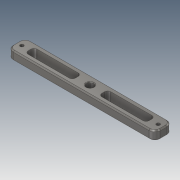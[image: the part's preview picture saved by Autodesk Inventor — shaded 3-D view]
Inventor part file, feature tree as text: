
AUTODESK INVENTOR PART (.ipt)
format: ipt  version: 2018.2 (Build 222227000, 227)  size: 164,864 bytes
history: native  units: mm
features: sketch x4, chamfer x3, extrude x2, mirror x1, hole x1, fillet x1
ambient origin geometry x8: Origin, YZ Plane, XZ Plane, XY Plane, X Axis, Y Axis, Z Axis, Center Point
bodies: Volumenkörper1 (feature_tree)
feature tree (12):
  extrude  "Grundkörper"  Depth=30.0mm
  extrude  "Ausschnitt_Gewichtsreduktion"  Depth=15.0mm
  mirror  "Spiegeln_Ausschnitt_Gewichtsreduktion"
  chamfer  "Fase_M6_Gewinde"  Distance=0.5mm Angle=45.0deg
  hole  "12H7_Bohrung"  [1 undecoded]
  fillet  "Abrundung"  Radius=80.0mm
  chamfer  "Fase_Allgemein"  Distance=5.0mm
  chamfer  "Fase_Bohrung"  Distance=15.0mm
  sketch  "Skizze1"  dims[d0=250.0mm d1=30.0mm]
  sketch  "Skizze2"  dims[d2=15.0mm d3=0.0mm d4=231.2mm]
  sketch  "Skizze3"  dims[d5=4.917mm d6=12.0mm d7=6.0mm d8=2.0mm d9=90.0deg d10=17.1mm d11=20.594885mm d12=0.5mm d13=2.0mm d14=45.0deg]
  sketch  "Skizze4"  dims[d15=10.0mm d16=15.0mm d17=80.0mm d18=5.0mm d19=15.0mm d20=0.0mm d21=2.0mm d22=2.0mm d23=45.0deg d24=12.0mm d25=6.0mm d26=4.0mm d27=2.0mm d28=90.0deg d29=8.0mm d30=20.594885mm d36=1.0mm d37=2.0mm d38=45.0deg]
note: 1 required parameter value undecoded (feature->parameter linkage not recoverable at this tier; creation-order binding heuristic only, values carry confidence <= 0.55)
